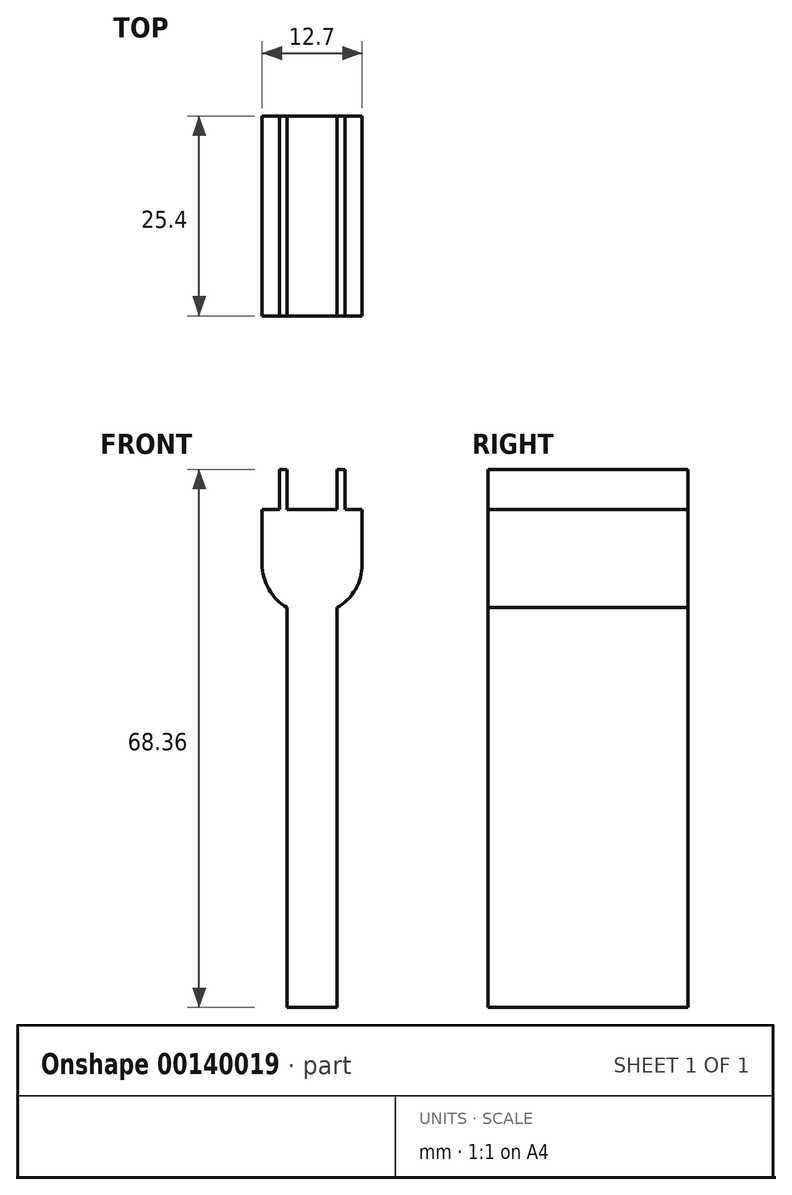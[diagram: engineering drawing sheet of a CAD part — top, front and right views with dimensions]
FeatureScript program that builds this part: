
annotation { "Feature Type Name" : "Feature", "Feature Type Description" : "" }
export const myFeature = defineFeature(function(context is Context, id is Id, definition is map)
    precondition{}
    {
        {
            var Q0;
            Q0=qCreatedBy(makeId("Front.planeOp"),FACE);
            var sketch = newSketch(context, id + "F0", { "sketchPlane" : qUnion([Q0])});
            skLineSegment(sketch, "E0.top", {"start": v(-3.18, -25.4) * mm, "end": v(3.17, -25.4) * mm});
            skLineSegment(sketch, "E0.left", {"start": v(-3.17, 25.4) * mm, "end": v(-3.18, -25.4) * mm});
            skLineSegment(sketch, "E0.right", {"start": v(3.18, 25.4) * mm, "end": v(3.17, -25.4) * mm});
            skPoint(sketch, "E0.middle", {"position": v(0, 0) * mm});
            skArc(sketch, "E1", {"start": v(-6.35, 30.9) * mm, "mid": v(-5.5, 27.72) * mm, "end": v(-3.18, 25.4) * mm});
            skPoint(sketch, "E1.centerSnap0", {"position": v(0, 25.4) * mm});
            skLineSegment(sketch, "E2", {"start": v(-6.35, 30.9) * mm, "end": v(-6.35, 37.88) * mm});
            skLineSegment(sketch, "E3", {"start": v(-6.35, 37.88) * mm, "end": v(-4.18, 37.88) * mm});
            skLineSegment(sketch, "E4", {"start": v(6.35, 37.88) * mm, "end": v(6.35, 30.9) * mm});
            skLineSegment(sketch, "E5.bottom", {"start": v(-4.18, 42.96) * mm, "end": v(-3.18, 42.96) * mm});
            skLineSegment(sketch, "E5.left", {"start": v(-4.18, 42.96) * mm, "end": v(-4.18, 37.88) * mm});
            skLineSegment(sketch, "E5.right", {"start": v(-3.18, 42.96) * mm, "end": v(-3.18, 37.88) * mm});
            skLineSegment(sketch, "E6", {"start": v(0, 37.88) * mm, "end": v(0, 0) * mm, "construction": true});
            skLineSegment(sketch, "E7.MirrorCS", {"start": v(4.17, 42.96) * mm, "end": v(3.17, 42.96) * mm});
            skLineSegment(sketch, "E8.MirrorCS", {"start": v(4.17, 42.96) * mm, "end": v(4.17, 37.88) * mm});
            skLineSegment(sketch, "E9.MirrorCS", {"start": v(3.17, 42.96) * mm, "end": v(3.17, 37.88) * mm});
            skArc(sketch, "E10.trimOffspring", {"start": v(3.18, 25.4) * mm, "mid": v(5.5, 27.72) * mm, "end": v(6.35, 30.9) * mm});
            skLineSegment(sketch, "E11.trimOffspring", {"start": v(-3.18, 37.88) * mm, "end": v(3.17, 37.88) * mm});
            skLineSegment(sketch, "E12.trimOffspring", {"start": v(4.17, 37.88) * mm, "end": v(6.35, 37.88) * mm});
            skSolve(sketch);
        }
        {
            var Q0;
            Q0=makeQuery(id+"F0.imprint","IMPRINT",FACE,{"disambiguationData":[TD([[makeQuery(id+"F0.imprint","IMPRINT",EDGE,{"derivedFrom":sQuery(id+"F0.wireOp",EDGE,"E0.top")}),1.0]])]});
            extrude(context, id + "F1", {"entities" : qUnion([Q0]), "depth" : 25.4 * mm});
        }
    });
